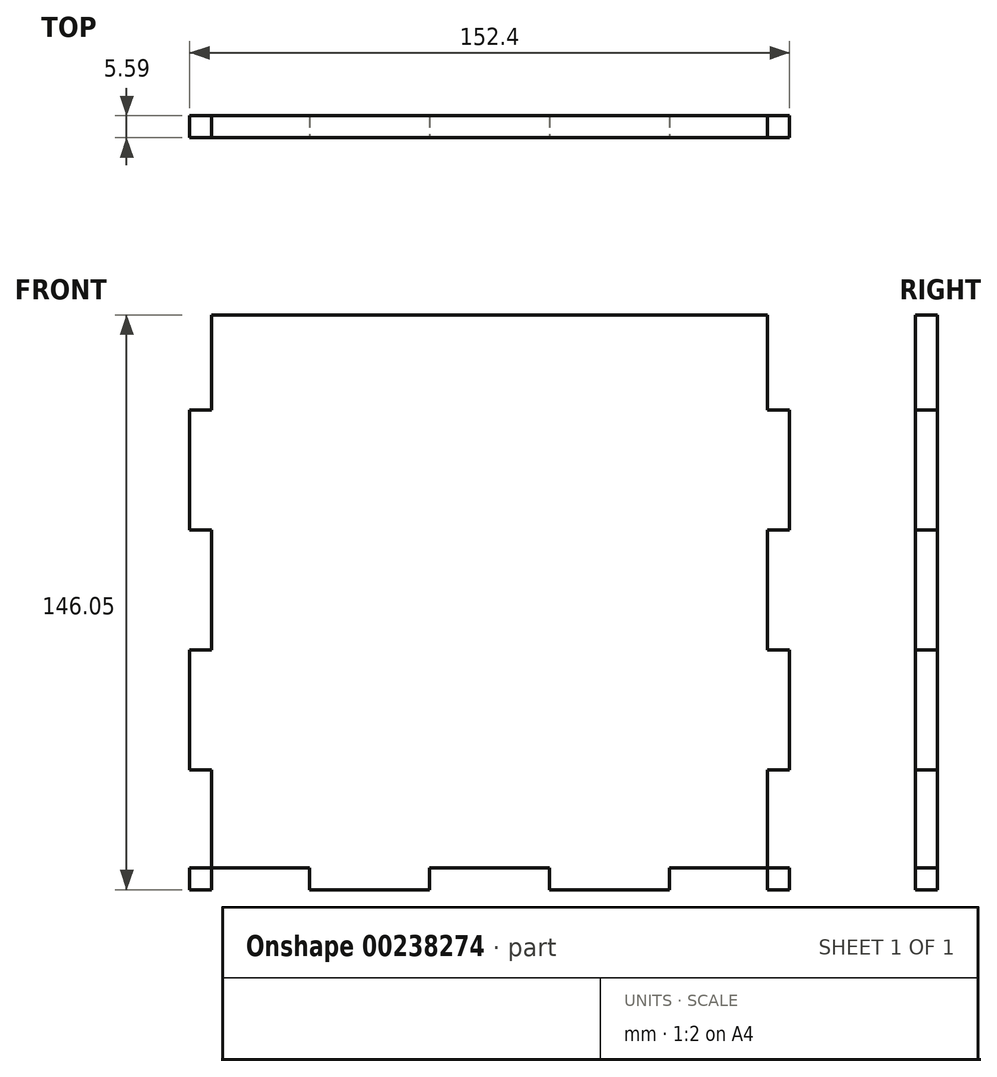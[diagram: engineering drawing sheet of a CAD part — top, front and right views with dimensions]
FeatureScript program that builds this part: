
annotation { "Feature Type Name" : "Feature", "Feature Type Description" : "" }
export const myFeature = defineFeature(function(context is Context, id is Id, definition is map)
    precondition{}
    {
        {
            var Q0;
            Q0=qCreatedBy(makeId("Front.planeOp"),FACE);
            var sketch = newSketch(context, id + "F0", { "sketchPlane" : qUnion([Q0])});
            skLineSegment(sketch, "E0.bottom", {"start": v(-76.2, 71.23) * mm, "end": v(76.2, 71.23) * mm});
            skLineSegment(sketch, "E0.top", {"start": v(-76.2, -74.82) * mm, "end": v(76.2, -74.82) * mm});
            skLineSegment(sketch, "E0.left", {"start": v(-76.2, 71.23) * mm, "end": v(-76.2, -74.82) * mm});
            skLineSegment(sketch, "E0.right", {"start": v(76.2, 71.23) * mm, "end": v(76.2, -74.82) * mm});
            skPoint(sketch, "E0.middle", {"position": v(0, -1.8) * mm});
            skSolve(sketch);
        }
        {
            var Q0;
            Q0=makeQuery(id+"F0.imprint","IMPRINT",FACE,{"disambiguationData":[TD([[makeQuery(id+"F0.imprint","IMPRINT",EDGE,{"derivedFrom":sQuery(id+"F0.wireOp",EDGE,"E0.bottom")}),-1.0]])]});
            extrude(context, id + "F1", {"entities" : qUnion([Q0]), "depth" : 5.6 * mm});
        }
        {
            var Q0;
            Q0=makeQuery(id+"F1.opExtrude","CAP_FACE",FACE,{"disambiguationData":[OSD([sQuery(id+"F0.wireOp",EDGE,"E0.bottom"),sQuery(id+"F0.wireOp",EDGE,"E0.top"),sQuery(id+"F0.wireOp",EDGE,"E0.left"),sQuery(id+"F0.wireOp",EDGE,"E0.right")])],"isStart":false});
            var sketch = newSketch(context, id + "F2", { "sketchPlane" : qUnion([Q0])});
            skLineSegment(sketch, "E1.bottom", {"start": v(-76.2, 71.23) * mm, "end": v(-70.61, 71.23) * mm});
            skLineSegment(sketch, "E1.top", {"start": v(-76.2, 47.1) * mm, "end": v(-70.61, 47.1) * mm});
            skLineSegment(sketch, "E1.left", {"start": v(-76.2, 71.23) * mm, "end": v(-76.2, 47.1) * mm});
            skLineSegment(sketch, "E1.right", {"start": v(-70.61, 71.23) * mm, "end": v(-70.61, 47.1) * mm});
            skLineSegment(sketch, "E2.bottom", {"start": v(-76.2, 16.62) * mm, "end": v(-70.61, 16.62) * mm});
            skLineSegment(sketch, "E2.top", {"start": v(-76.2, -13.86) * mm, "end": v(-70.61, -13.86) * mm});
            skLineSegment(sketch, "E2.left", {"start": v(-76.2, 16.62) * mm, "end": v(-76.2, -13.86) * mm});
            skLineSegment(sketch, "E2.right", {"start": v(-70.61, 16.62) * mm, "end": v(-70.61, -13.86) * mm});
            skLineSegment(sketch, "E3.bottom", {"start": v(-76.2, -74.82) * mm, "end": v(-70.61, -74.82) * mm});
            skLineSegment(sketch, "E3.top", {"start": v(-76.2, -44.34) * mm, "end": v(-70.61, -44.34) * mm});
            skLineSegment(sketch, "E3.left", {"start": v(-76.2, -74.82) * mm, "end": v(-76.2, -44.34) * mm});
            skLineSegment(sketch, "E3.right", {"start": v(-70.61, -74.82) * mm, "end": v(-70.61, -44.34) * mm});
            skLineSegment(sketch, "E4.bottom", {"start": v(76.2, -74.82) * mm, "end": v(70.61, -74.82) * mm});
            skLineSegment(sketch, "E4.top", {"start": v(76.2, -44.34) * mm, "end": v(70.61, -44.34) * mm});
            skLineSegment(sketch, "E4.left", {"start": v(76.2, -74.82) * mm, "end": v(76.2, -44.34) * mm});
            skLineSegment(sketch, "E4.right", {"start": v(70.61, -74.82) * mm, "end": v(70.61, -44.34) * mm});
            skLineSegment(sketch, "E5.bottom", {"start": v(76.2, -13.86) * mm, "end": v(70.61, -13.86) * mm});
            skLineSegment(sketch, "E5.top", {"start": v(76.2, 16.62) * mm, "end": v(70.61, 16.62) * mm});
            skLineSegment(sketch, "E5.left", {"start": v(76.2, -13.86) * mm, "end": v(76.2, 16.62) * mm});
            skLineSegment(sketch, "E5.right", {"start": v(70.61, -13.86) * mm, "end": v(70.61, 16.62) * mm});
            skLineSegment(sketch, "E6.bottom", {"start": v(76.2, 71.23) * mm, "end": v(70.61, 71.23) * mm});
            skLineSegment(sketch, "E6.top", {"start": v(76.2, 47.1) * mm, "end": v(70.61, 47.1) * mm});
            skLineSegment(sketch, "E6.left", {"start": v(76.2, 71.23) * mm, "end": v(76.2, 47.1) * mm});
            skLineSegment(sketch, "E6.right", {"start": v(70.61, 71.23) * mm, "end": v(70.61, 47.1) * mm});
            skLineSegment(sketch, "E7.bottom", {"start": v(-76.2, -74.82) * mm, "end": v(-45.72, -74.82) * mm});
            skLineSegment(sketch, "E7.top", {"start": v(-76.2, -69.24) * mm, "end": v(-45.72, -69.24) * mm});
            skLineSegment(sketch, "E7.left", {"start": v(-76.2, -74.82) * mm, "end": v(-76.2, -69.24) * mm});
            skLineSegment(sketch, "E7.right", {"start": v(-45.72, -74.82) * mm, "end": v(-45.72, -69.24) * mm});
            skLineSegment(sketch, "E8.bottom", {"start": v(-15.24, -74.82) * mm, "end": v(15.24, -74.82) * mm});
            skLineSegment(sketch, "E8.top", {"start": v(-15.24, -69.24) * mm, "end": v(15.24, -69.24) * mm});
            skLineSegment(sketch, "E8.left", {"start": v(-15.24, -74.82) * mm, "end": v(-15.24, -69.24) * mm});
            skLineSegment(sketch, "E8.right", {"start": v(15.24, -74.82) * mm, "end": v(15.24, -69.24) * mm});
            skLineSegment(sketch, "E9.bottom", {"start": v(76.2, -74.82) * mm, "end": v(45.72, -74.82) * mm});
            skLineSegment(sketch, "E9.top", {"start": v(76.2, -69.24) * mm, "end": v(45.72, -69.24) * mm});
            skLineSegment(sketch, "E9.left", {"start": v(76.2, -74.82) * mm, "end": v(76.2, -69.24) * mm});
            skLineSegment(sketch, "E9.right", {"start": v(45.72, -74.82) * mm, "end": v(45.72, -69.24) * mm});
            skSolve(sketch);
        }
        {
            var Q0;
            Q0=makeQuery(id+"F2.imprint","IMPRINT",FACE,{"disambiguationData":[TD([[makeQuery(id+"F2.imprint","IMPRINT",EDGE,{"derivedFrom":sQuery(id+"F2.wireOp",EDGE,"E1.bottom")}),-1.0]])]});
            var Q1;
            Q1=makeQuery(id+"F2.imprint","IMPRINT",FACE,{"disambiguationData":[TD([[makeQuery(id+"F2.imprint","IMPRINT",EDGE,{"derivedFrom":sQuery(id+"F2.wireOp",EDGE,"E2.bottom")}),-1.0]])]});
            var Q2;
            {var subQ0=sQuery(id+"F2.wireOp",EDGE,"E3.top");Q2=makeQuery(id+"F2.imprint","IMPRINT",FACE,{"disambiguationData":[TD([[makeQuery(id+"F2.imprint","IMPRINT",EDGE,{"derivedFrom":subQ0}),-1.0]])]});}
            var Q3;
            {var subQ5=sQuery(id+"F2.wireOp",EDGE,"E7.right");Q3=makeQuery(id+"F2.imprint","IMPRINT",FACE,{"disambiguationData":[TD([[makeQuery(id+"F2.imprint","IMPRINT",EDGE,{"derivedFrom":subQ5}),1.0]])]});}
            var Q4;
            {var subQ5=sQuery(id+"F2.wireOp",EDGE,"E7.left");Q4=makeQuery(id+"F2.imprint","IMPRINT",FACE,{"disambiguationData":[TD([[makeQuery(id+"F2.imprint","IMPRINT",EDGE,{"derivedFrom":subQ5}),1.0]])]});}
            var Q5;
            Q5=makeQuery(id+"F2.imprint","IMPRINT",FACE,{"disambiguationData":[TD([[makeQuery(id+"F2.imprint","IMPRINT",EDGE,{"derivedFrom":sQuery(id+"F2.wireOp",EDGE,"E8.bottom")}),1.0]])]});
            var Q6;
            {var subQ5=sQuery(id+"F2.wireOp",EDGE,"E9.right");Q6=makeQuery(id+"F2.imprint","IMPRINT",FACE,{"disambiguationData":[TD([[makeQuery(id+"F2.imprint","IMPRINT",EDGE,{"derivedFrom":subQ5}),-1.0]])]});}
            var Q7;
            {var subQ5=sQuery(id+"F2.wireOp",EDGE,"E9.left");Q7=makeQuery(id+"F2.imprint","IMPRINT",FACE,{"disambiguationData":[TD([[makeQuery(id+"F2.imprint","IMPRINT",EDGE,{"derivedFrom":subQ5}),-1.0]])]});}
            var Q8;
            {var subQ0=sQuery(id+"F2.wireOp",EDGE,"E4.top");Q8=makeQuery(id+"F2.imprint","IMPRINT",FACE,{"disambiguationData":[TD([[makeQuery(id+"F2.imprint","IMPRINT",EDGE,{"derivedFrom":subQ0}),1.0]])]});}
            var Q9;
            Q9=makeQuery(id+"F2.imprint","IMPRINT",FACE,{"disambiguationData":[TD([[makeQuery(id+"F2.imprint","IMPRINT",EDGE,{"derivedFrom":sQuery(id+"F2.wireOp",EDGE,"E5.bottom")}),-1.0]])]});
            var Q10;
            Q10=makeQuery(id+"F2.imprint","IMPRINT",FACE,{"disambiguationData":[TD([[makeQuery(id+"F2.imprint","IMPRINT",EDGE,{"derivedFrom":sQuery(id+"F2.wireOp",EDGE,"E6.bottom")}),-1.0]])]});
            extrude(context, id + "F3", {"entities" : qUnion([Q0, Q1, Q2, Q3, Q4, Q5, Q6, Q7, Q8, Q9, Q10]), "operationType" : NewBodyOperationType.REMOVE, "endBound" : BoundingType.THROUGH_ALL, "oppositeDirection" : true, "depth" : 25.4 * mm});
        }
    });
